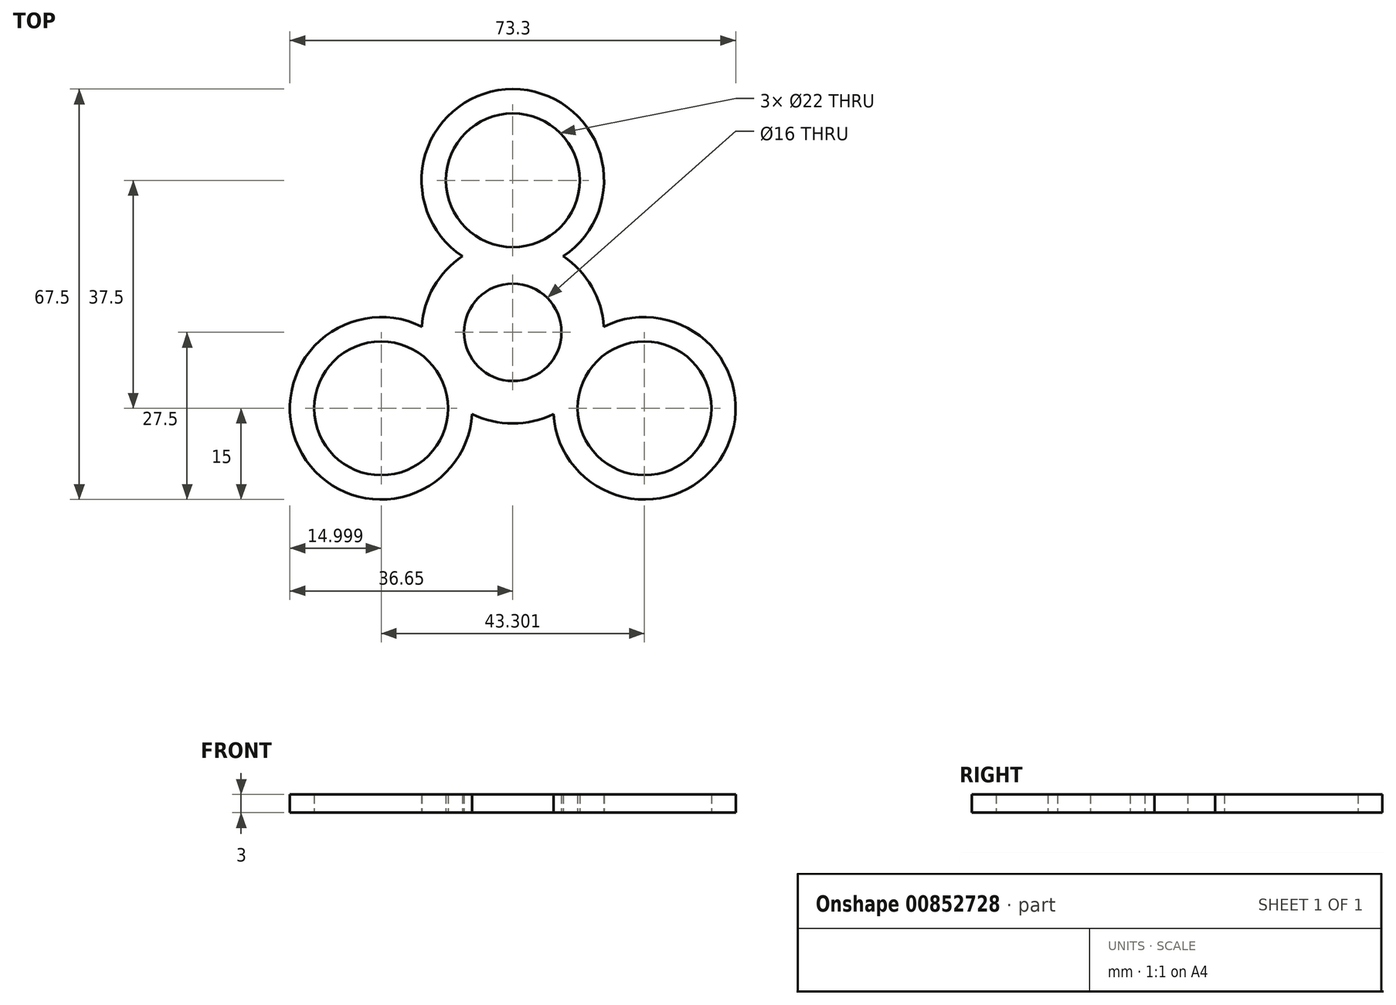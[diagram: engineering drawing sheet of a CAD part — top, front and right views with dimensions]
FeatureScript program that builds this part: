
annotation { "Feature Type Name" : "Feature", "Feature Type Description" : "" }
export const myFeature = defineFeature(function(context is Context, id is Id, definition is map)
    precondition{}
    {
        {
            var Q0;
            Q0=qCreatedBy(makeId("Top.planeOp"),FACE);
            var sketch = newSketch(context, id + "F0", { "sketchPlane" : qUnion([Q0])});
            skCircle(sketch, "E0", {"center": v(0, 0) * mm, "radius": 8 * mm});
            skArc(sketch, "E1", {"start": v(-8.3, 12.5) * mm, "mid": v(-13, 7.5) * mm, "end": v(-14.97, 0.93) * mm});
            skLineSegment(sketch, "E2", {"start": v(0, 0) * mm, "end": v(0, 25) * mm});
            skCircle(sketch, "E3", {"center": v(0, 25) * mm, "radius": 11 * mm});
            skArc(sketch, "E4", {"start": v(8.3, 12.5) * mm, "mid": v(0, 40) * mm, "end": v(-8.3, 12.5) * mm});
            skCircle(sketch, "E5.1.0", {"center": v(-21.65, -12.5) * mm, "radius": 11 * mm});
            skArc(sketch, "E5.1.1", {"start": v(-14.97, 0.93) * mm, "mid": v(-34.64, -20) * mm, "end": v(-6.68, -13.43) * mm});
            skCircle(sketch, "E5.2.0", {"center": v(21.65, -12.5) * mm, "radius": 11 * mm});
            skArc(sketch, "E5.2.1", {"start": v(6.68, -13.43) * mm, "mid": v(34.64, -20) * mm, "end": v(14.97, 0.93) * mm});
            skArc(sketch, "E6.trimOffspring", {"start": v(-6.68, -13.43) * mm, "mid": v(0, -15) * mm, "end": v(6.68, -13.43) * mm});
            skArc(sketch, "E7.trimOffspring", {"start": v(14.97, 0.93) * mm, "mid": v(13, 7.5) * mm, "end": v(8.3, 12.5) * mm});
            skSolve(sketch);
        }
        {
            var Q0;
            Q0 = qSketchRegion(id + "F0", true);
            extrude(context, id + "F1", {"entities" : qUnion([Q0]), "depth" : 3 * mm, "offsetDistance" : 25 * mm});
        }
    });
